# Revit family: Duomo 4.0
name_source: partatom
category: Lighting Fixtures
units: mm (PartAtom-declared; Revit-internal decimal feet)

## family parameters
Always vertical = No
Cut with Voids When Loaded = No
Light Source = No
OmniClass Number = 23.80.70.00
OmniClass Title = Lighting
Part Type = Normal
Room Calculation Point = Yes
Round Connector Dimension = Use Diameter
Shared = No
Work Plane-Based = No

## types (8) — shared parameters
Apparent Load Phase 1 = 56 W
Base = L&L_Anticorodal aluminium
Body = L&L_Anticorodal aluminium
CRI = >90 (also available: CRI 80 - ref. URL Technical sheet)
Code = -
Connector = L&L_Plastic
Control system = DALI, ON/OFF
Cutout dimensions = -
Delivered lumen output = 3964 lm (3000K, 30°, CRI 90), 4284 lm (3000K, 30°, CRI 80)
Description = Projector for indoor applications
Energy efficiency class = A A+ A++
Features = electrical wiring simplified by the ability to connect the electrical cables directly to the connector
Height mm = 166 mm  [stored 0.544619 ft]
IP = IP54
LED Colour = 3000K (also available: 2700K and 4000K - ref. URL Technical sheet)
Length mm = 396 mm  [stored 1.29921 ft]
Lens = L&L_Tempered extra-clear glass
Lumen output at source = 4886 lm (3000K, CRI 90), 5280 lm (3000K, CRI 80)
Manufacturer = L&L Luce&Light
Material = body and arm in Anticorodal aluminium,  screen in serigraphed, tempered, extra-clear glass
Model = Duomo 4.0
Mounting = surface mounted (ceiling, wall, floor)
No. and type of led = 12 power LEDs High Intensity, 3-step MacAdam, 50 000h L90 B10 (Ta 25°C)
Notes = available on request with adapter for Eurostandard track and in 1–10V or PUSH version, or with Bluetooth control
Power = 56W
Power cables = -
Power supply = 230Vac
230Vac
Power supply unit = built-in
Screw = L&L_Steel inox AISI 316L
URL = https://www.lucelight.it
URL Accessories and power supply units = https://www.lucelight.it
URL Catalogue = -
URL DXF = https://www.lucelight.it
URL Description = https://www.lucelight.it
URL General code = https://www.lucelight.it
URL IES Photometric file = https://www.lucelight.it
URL Image = https://www.lucelight.it
URL Technical sheet = -
Vertical rotation max = 220.00°
Weight kg = 4.50 kg
Width mm = 50 mm  [stored 0.164042 ft]
Wiring = parallel
zero-valued in all types: Default Elevation

## per-type parameters (varying)
| type | Light Source | Optics |
| DUOMO 4.0 J 43° (3000K 56W 230Vac) | Light Source_40 : J 43° | 43° |
| DUOMO 4.0 K 63° (3000K 56W 230Vac) | Light Source_40 : K 63° | 63° |
| DUOMO 4.0 L 35° (3000K 56W 230Vac) | Light Source_40 : L 35° | 35° |
| DUOMO 4.0 M 30° (3000K 56W 230Vac) | Light Source_40 : M 30° | 30° |
| DUOMO 4.0 S 14° (3000K 56W 230Vac) | Light Source_40 : S 14° | 14° |
| DUOMO 4.0 T 10° (3000K 56W 230Vac) | Light Source_40 : T 10° | 10° |
| DUOMO 4.0 W 18°x44° (3000K 56W 230Vac) | Light Source_40 : W 18°x44° | 18°x44° |
| DUOMO 4.0 X 44°x18° (3000K 56W 230Vac) | Light Source_40 : X 44°x18° | 44°x18° |

note: [stored X ft] marks values corroborated as IEEE doubles in the binary element streams (Revit-internal decimal feet)

## geometry (parser evidence)
native form markers: Sweep x15
no freeform markers — native parametric forms only
